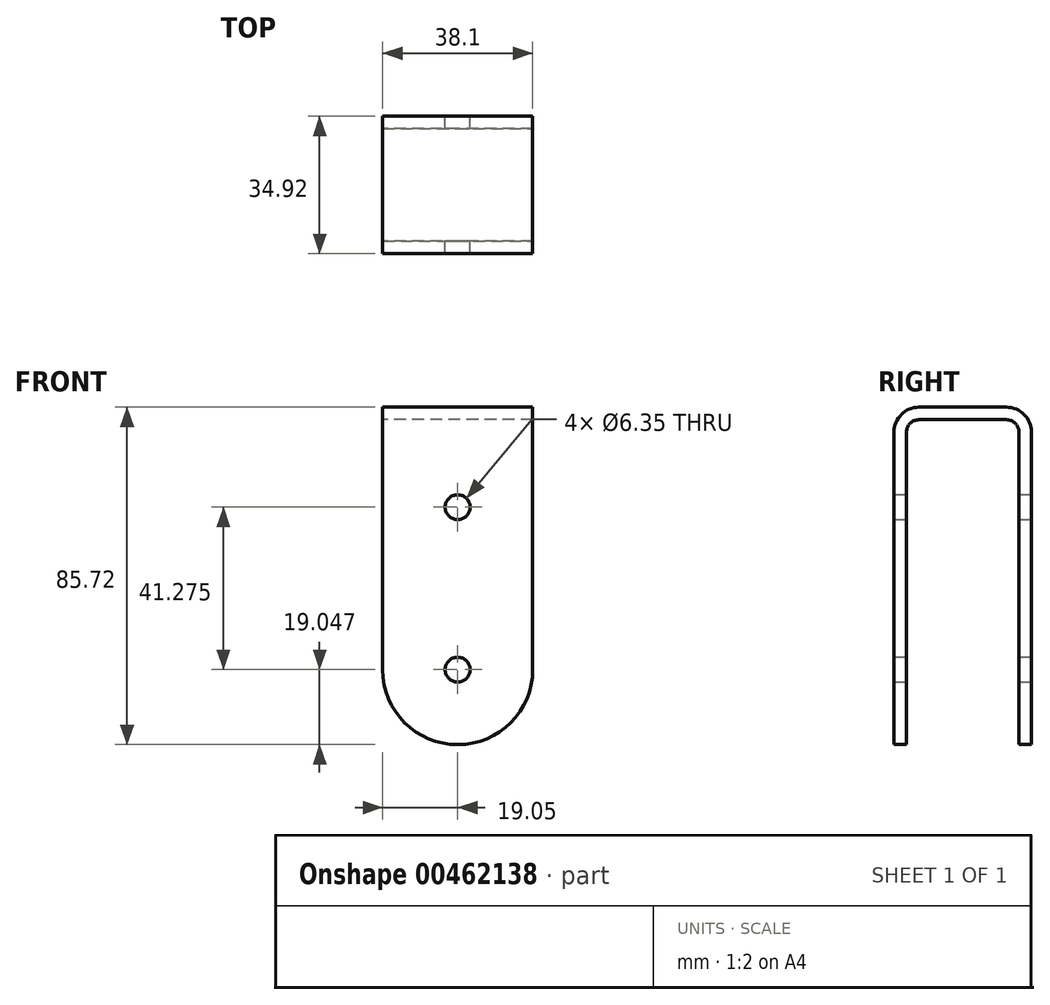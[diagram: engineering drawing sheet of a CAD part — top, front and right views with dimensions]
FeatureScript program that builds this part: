
annotation { "Feature Type Name" : "Feature", "Feature Type Description" : "" }
export const myFeature = defineFeature(function(context is Context, id is Id, definition is map)
    precondition{}
    {
        {
            var Q0;
            Q0=qCreatedBy(makeId("Right.planeOp"),FACE);
            var sketch = newSketch(context, id + "F0", { "sketchPlane" : qUnion([Q0])});
            skLineSegment(sketch, "E0.top", {"start": v(-1.59, 77.79) * mm, "end": v(26.99, 77.79) * mm});
            skLineSegment(sketch, "E0.left", {"start": v(-1.59, -4.76) * mm, "end": v(-1.59, 77.79) * mm});
            skLineSegment(sketch, "E0.right", {"start": v(26.99, -4.76) * mm, "end": v(26.99, 77.79) * mm});
            skLineSegment(sketch, "E1.0", {"start": v(-4.76, -4.76) * mm, "end": v(-4.76, 80.96) * mm});
            skLineSegment(sketch, "E1.1", {"start": v(-4.76, -4.76) * mm, "end": v(-1.59, -4.76) * mm});
            skLineSegment(sketch, "E1.2", {"start": v(30.16, -4.76) * mm, "end": v(30.16, 80.96) * mm});
            skLineSegment(sketch, "E1.3", {"start": v(-4.76, 80.96) * mm, "end": v(30.16, 80.96) * mm});
            skLineSegment(sketch, "E2.trimOffspring", {"start": v(26.99, -4.76) * mm, "end": v(30.16, -4.76) * mm});
            skSolve(sketch);
        }
        {
            var Q0;
            Q0 = qSketchRegion(id + "F0", true);
            extrude(context, id + "F1", {"entities" : qUnion([Q0]), "depth" : 38.1 * mm});
        }
        {
            var Q0;
            Q0=makeQuery(id+"F1.opExtrude","SWEPT_EDGE",EDGE,{"disambiguationData":[OSD([sQuery(id+"F0.wireOp",EDGE,"E0.top"),sQuery(id+"F0.wireOp",EDGE,"E0.right")])]});
            var Q1;
            Q1=makeQuery(id+"F1.opExtrude","SWEPT_EDGE",EDGE,{"disambiguationData":[OSD([sQuery(id+"F0.wireOp",EDGE,"E0.top"),sQuery(id+"F0.wireOp",EDGE,"E0.left")])]});
            fillet(context, id + "F2", {"entities" : qUnion([Q0, Q1]), "radius" : 3.17 * mm, "tangentPropagation" : true, "allowEdgeOverflow" : false});
        }
        {
            var Q0;
            Q0=makeQuery(id+"F1.opExtrude","SWEPT_EDGE",EDGE,{"disambiguationData":[OSD([sQuery(id+"F0.wireOp",EDGE,"E1.2"),sQuery(id+"F0.wireOp",EDGE,"E1.3")])]});
            var Q1;
            Q1=makeQuery(id+"F1.opExtrude","SWEPT_EDGE",EDGE,{"disambiguationData":[OSD([sQuery(id+"F0.wireOp",EDGE,"E1.0"),sQuery(id+"F0.wireOp",EDGE,"E1.3")])]});
            fillet(context, id + "F3", {"entities" : qUnion([Q0, Q1]), "radius" : 6.35 * mm, "tangentPropagation" : true, "allowEdgeOverflow" : false});
        }
        {
            var Q0;
            Q0=makeQuery(id+"F1.opExtrude","CAP_EDGE",EDGE,{"disambiguationData":[OSD([sQuery(id+"F0.wireOp",EDGE,"E2.trimOffspring")])],"isStart":false});
            var Q1;
            Q1=makeQuery(id+"F1.opExtrude","CAP_EDGE",EDGE,{"disambiguationData":[OSD([sQuery(id+"F0.wireOp",EDGE,"E2.trimOffspring")])],"isStart":true});
            var Q2;
            Q2=makeQuery(id+"F1.opExtrude","CAP_EDGE",EDGE,{"disambiguationData":[OSD([sQuery(id+"F0.wireOp",EDGE,"E1.1")])],"isStart":false});
            var Q3;
            Q3=makeQuery(id+"F1.opExtrude","CAP_EDGE",EDGE,{"disambiguationData":[OSD([sQuery(id+"F0.wireOp",EDGE,"E1.1")])],"isStart":true});
            fillet(context, id + "F4", {"entities" : qUnion([Q0, Q1, Q2, Q3]), "radius" : 19.05 * mm, "tangentPropagation" : true, "allowEdgeOverflow" : false});
        }
        {
            var Q0;
            Q0=makeQuery(id+"F1.opExtrude","SWEPT_FACE",FACE,{"disambiguationData":[OSD([sQuery(id+"F0.wireOp",EDGE,"E1.2")])]});
            var sketch = newSketch(context, id + "F5", { "sketchPlane" : qUnion([Q0])});
            skCircle(sketch, "E3", {"center": v(-19.05, 14.29) * mm, "radius": 3.18 * mm});
            skLineSegment(sketch, "E4", {"start": v(-19.05, 14.29) * mm, "end": v(-19.05, 109.83) * mm, "construction": true});
            skPoint(sketch, "E4.endSnap0", {"position": v(-19.05, 74.61) * mm});
            skCircle(sketch, "E5", {"center": v(-19.05, 55.56) * mm, "radius": 3.18 * mm});
            skSolve(sketch);
        }
        {
            var Q0;
            Q0 = qSketchRegion(id + "F5", true);
            extrude(context, id + "F6", {"entities" : qUnion([Q0]), "operationType" : NewBodyOperationType.REMOVE, "endBound" : BoundingType.THROUGH_ALL, "oppositeDirection" : true, "depth" : 25.4 * mm});
        }
    });
